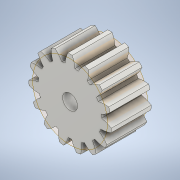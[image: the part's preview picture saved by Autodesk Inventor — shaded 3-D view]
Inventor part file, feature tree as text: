
AUTODESK INVENTOR PART (.ipt)
format: ipt  version: 2021 (Build 250183000, 183)  size: 223,232 bytes
history: native  units: mm (DEFAULTED — no unit token found)
features: plane x3, other x3, sketch x3, extrude x1, hole x1
ambient origin geometry x8: Origin, YZ Plane, XZ Plane, XY Plane, X Axis, Y Axis, Z Axis, Center Point
bodies: Solid1 (feature_tree)
feature tree (11):
  extrude  "Extrusion1"  Depth=8.0mm TaperAngle=0.0deg
  plane  "Work Plane2"
  plane  "Work Plane8"
  plane  "Work Plane9"
  other  "Spur Gear"
  hole  "Hole1"  [1 undecoded]
  sketch  "Sketch1"  dims[d0=16.6mm d1=8.0mm d2=0.0mm]
  sketch  "Sketch2"  dims[d3=15.0mm d4=10.0mm d5=0.0mm]
  other  "Srf1"
  sketch  "Sketch3"  dims[d16=22.5mm d17=0.0mm d34=2.094395mm d39=0.0mm d41=0.0mm d43=22.5mm d46=22.5mm d47=0.0mm d48=0.0mm d49=3.0mm d50=3.0mm d51=6.0mm d52=4.0mm d53=2.0mm d54=90.0deg d55=8.0mm d56=20.594885mm]
  other  "Pitch Diameter"
note: 1 required parameter value undecoded (feature->parameter linkage not recoverable at this tier; creation-order binding heuristic only, values carry confidence <= 0.55)
